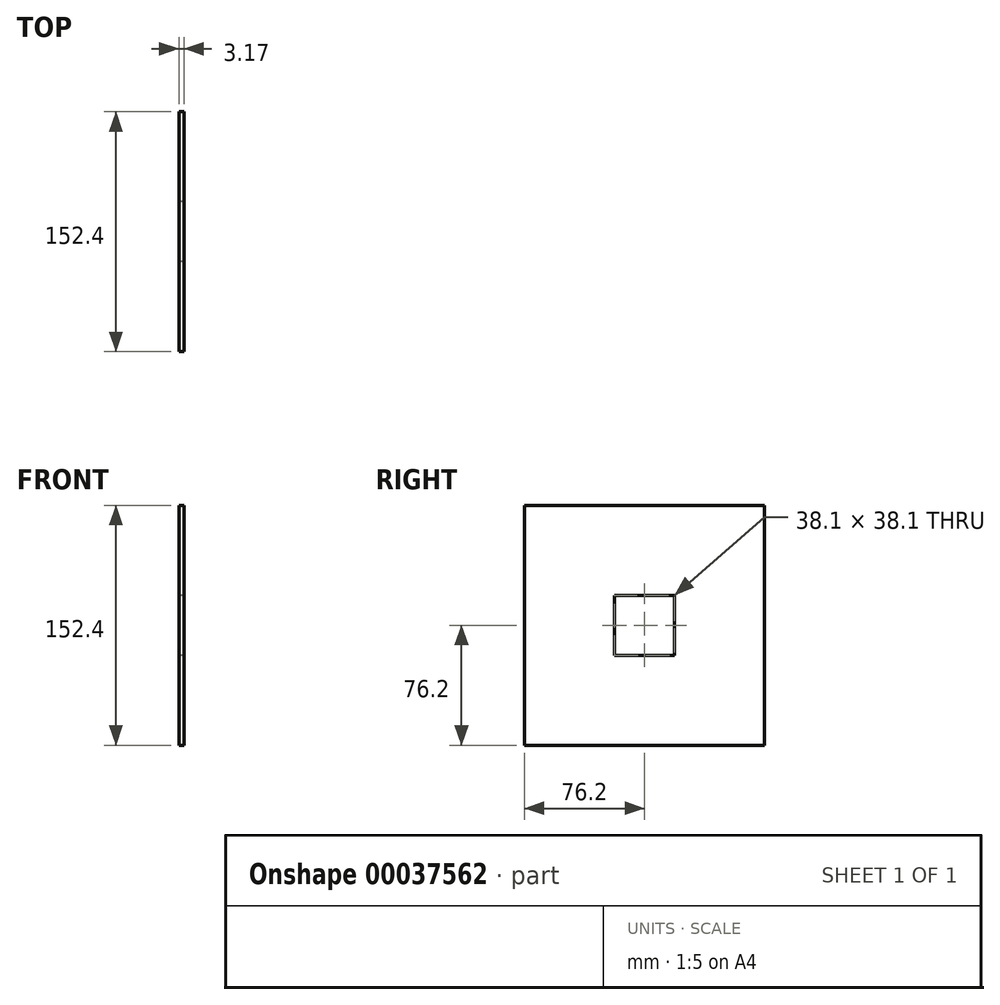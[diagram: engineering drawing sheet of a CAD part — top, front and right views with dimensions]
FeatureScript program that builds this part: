
annotation { "Feature Type Name" : "Feature", "Feature Type Description" : "" }
export const myFeature = defineFeature(function(context is Context, id is Id, definition is map)
    precondition{}
    {
        {
            var Q0;
            Q0=qCreatedBy(makeId("Right.planeOp"),FACE);
            var sketch = newSketch(context, id + "F0", { "sketchPlane" : qUnion([Q0])});
            skLineSegment(sketch, "E0.rect.bottom", {"start": v(76.2, -69.85) * mm, "end": v(-76.2, -69.85) * mm});
            skLineSegment(sketch, "E0.rect.top", {"start": v(76.2, 82.55) * mm, "end": v(-76.2, 82.55) * mm});
            skLineSegment(sketch, "E0.rect.left", {"start": v(76.2, -69.85) * mm, "end": v(76.2, 82.55) * mm});
            skLineSegment(sketch, "E0.rect.right", {"start": v(-76.2, -69.85) * mm, "end": v(-76.2, 82.55) * mm});
            skPoint(sketch, "E0.rect.middle", {"position": v(0, 6.35) * mm});
            skLineSegment(sketch, "E1.rect.bottom", {"start": v(19.05, -12.7) * mm, "end": v(-19.05, -12.7) * mm});
            skLineSegment(sketch, "E1.rect.top", {"start": v(19.05, 25.4) * mm, "end": v(-19.05, 25.4) * mm});
            skLineSegment(sketch, "E1.rect.left", {"start": v(19.05, -12.7) * mm, "end": v(19.05, 25.4) * mm});
            skLineSegment(sketch, "E1.rect.right", {"start": v(-19.05, -12.7) * mm, "end": v(-19.05, 25.4) * mm});
            skSolve(sketch);
        }
        {
            var Q0;
            Q0=makeQuery(id+"F0.imprint","IMPRINT",FACE,{"disambiguationData":[TD([[makeQuery(id+"F0.imprint","IMPRINT",EDGE,{"derivedFrom":sQuery(id+"F0.wireOp",EDGE,"E0.rect.bottom")}),-1.0]])]});
            extrude(context, id + "F1", {"entities" : qUnion([Q0]), "depth" : 3.17 * mm});
        }
    });
